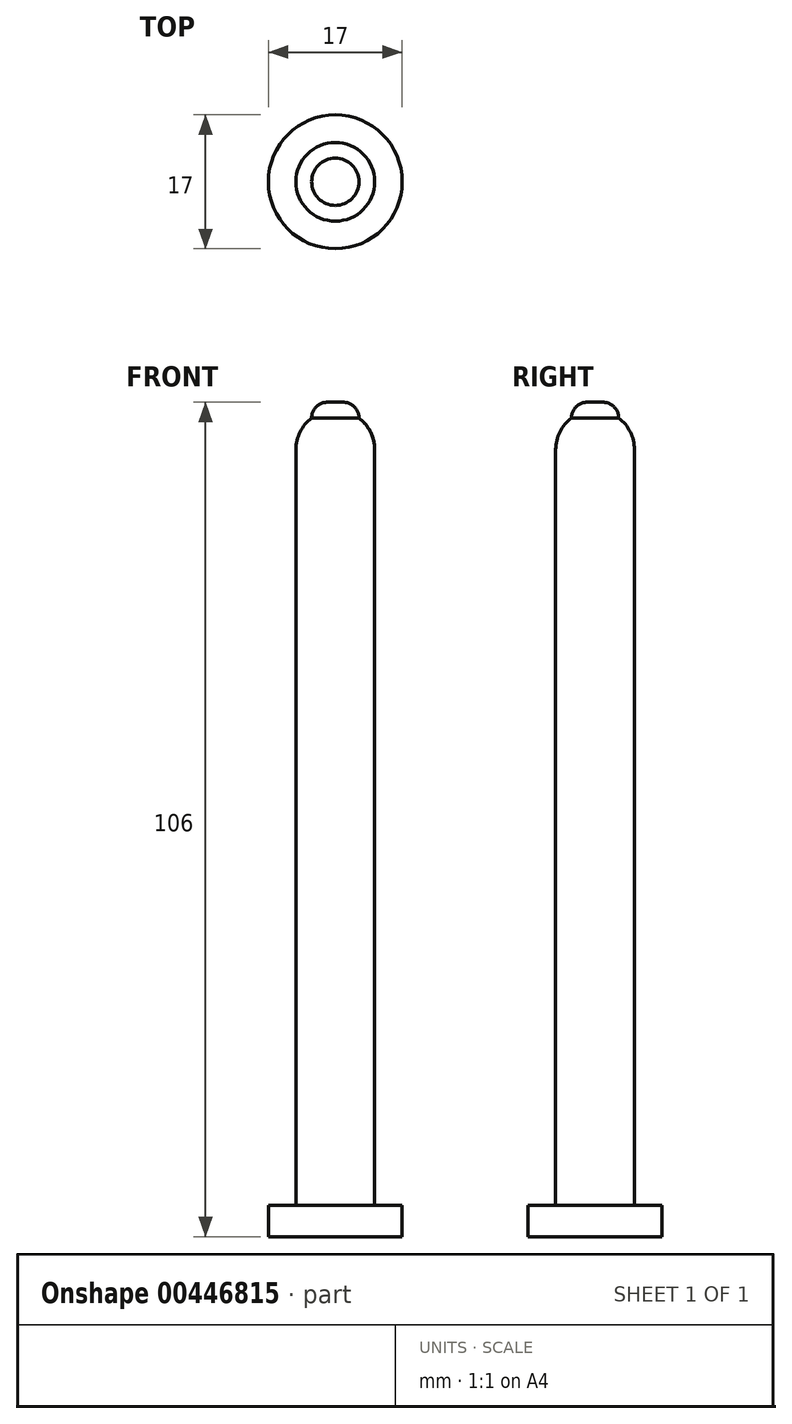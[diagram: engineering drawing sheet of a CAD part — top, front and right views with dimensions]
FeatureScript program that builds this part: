
annotation { "Feature Type Name" : "Feature", "Feature Type Description" : "" }
export const myFeature = defineFeature(function(context is Context, id is Id, definition is map)
    precondition{}
    {
        {
            var Q0;
            Q0=qCreatedBy(makeId("Top.planeOp"),FACE);
            var sketch = newSketch(context, id + "F0", { "sketchPlane" : qUnion([Q0])});
            skCircle(sketch, "E0", {"center": v(0, 0) * mm, "radius": 8.5 * mm});
            skSolve(sketch);
        }
        {
            var Q0;
            Q0=qSketchRegion(id+"F0",true);
            extrude(context, id + "F1", {"entities" : qUnion([Q0]), "depth" : 4 * mm});
        }
        {
            var Q0;
            Q0=qCreatedBy(makeId("Top.planeOp"),FACE);
            var sketch = newSketch(context, id + "F2", { "sketchPlane" : qUnion([Q0])});
            skCircle(sketch, "E1", {"center": v(0, 0) * mm, "radius": 5 * mm});
            skSolve(sketch);
        }
        {
            var Q0;
            Q0=qSketchRegion(id+"F2",true);
            extrude(context, id + "F3", {"entities" : qUnion([Q0]), "operationType" : NewBodyOperationType.ADD, "depth" : 100 * mm});
        }
        {
            var Q0;
            Q0=qCreatedBy(makeId("Right.planeOp"),FACE);
            var sketch = newSketch(context, id + "F4", { "sketchPlane" : qUnion([Q0])});
            skLineSegment(sketch, "E2", {"start": v(0, 100) * mm, "end": v(5, 100) * mm});
            skArc(sketch, "E3", {"start": v(5, 100) * mm, "mid": v(3.54, 103.54) * mm, "end": v(0, 105) * mm});
            skLineSegment(sketch, "E4", {"start": v(0, 106) * mm, "end": v(1, 106) * mm});
            skLineSegment(sketch, "E5", {"start": v(3, 104) * mm, "end": v(0, 104) * mm});
            skLineSegment(sketch, "E6", {"start": v(0, 106) * mm, "end": v(0, 100) * mm});
            skArc(sketch, "E7", {"start": v(3, 104) * mm, "mid": v(2.41, 105.41) * mm, "end": v(1, 106) * mm});
            skSolve(sketch);
        }
        {
            var Q0;
            {var subQ0=sQuery(id+"F4.wireOp",EDGE,"E2");Q0=makeQuery(id+"F4.imprint","IMPRINT",FACE,{"disambiguationData":[TD([[makeQuery(id+"F4.imprint","IMPRINT",EDGE,{"derivedFrom":subQ0}),1.0]])]});}
            var Q1;
            {var subQ4=sQuery(id+"F4.wireOp",EDGE,"E4");Q1=makeQuery(id+"F4.imprint","IMPRINT",FACE,{"disambiguationData":[TD([[makeQuery(id+"F4.imprint","IMPRINT",EDGE,{"derivedFrom":subQ4}),-1.0]])]});}
            var Q2;
            {var subQ3=sQuery(id+"F4.wireOp",EDGE,"E5");Q2=makeQuery(id+"F4.imprint","IMPRINT",FACE,{"disambiguationData":[TD([[makeQuery(id+"F4.imprint","IMPRINT",EDGE,{"derivedFrom":subQ3}),-1.0]])]});}
            var Q3;
            Q3=sQuery(id+"F4.wireOp",EDGE,"E6");
            revolve(context, id + "F5", {"operationType" : NewBodyOperationType.ADD, "entities" : qUnion([Q0, Q1, Q2]), "axis" : qUnion([Q3]), "revolveType" : RevolveType.FULL});
        }
    });
